# Revit family: IS_iLifeA_T4519_BIM_NL
name_source: partatom
category: Plumbing Fixtures
units: mm (PartAtom-declared; Revit-internal decimal feet)

## family parameters
Always vertical = No
Cut with Voids When Loaded = No
OmniClass Number = 23.45.05.14.14
OmniClass Title = Sinks/Lavatories
Part Type = Normal
Room Calculation Point = No
Round Connector Dimension = Use Diameter
Shared = No
Work Plane-Based = No

## types (2) — shared parameters
Accessories = https://www.idealstandard.nl
Afmetingen = 288 x 360 x 195mm
AfstandsEenheid = Millimeter
Afwerking = Weiß
AreaMeasurement = internal
AreaUnits = Millimeter
Artikelnummer = T451901
Artikelomschrijving = I.life A semi-voetstuk wit - Wit
Artikelreferentie = I.life A semipedestal white
Auteur = Ideal Standard
BIMObjectName = IS_IdealStandard_Pedestalwashbasins_I.life_T4519
BarCode = 8014140485872
Beschrijvinggarantie = Herstellergarantie
Bestanddelen = Halbpodest weiß
BimObjectNaam = IS_IdealStandard_Pedestalwashbasins_I.life_T4519
Brand url = https://www.idealstandard.nl
Color = Weiß
ConnectionType = Plumbing
CurrencyUnit = €
CurrentRevision = 1
Date of publishing = 28/06/2021
Description = I.life A semi-voetstuk wit - Wit
DurationUnit = Years
DuurEenheid = Jaar
Edition number = 1
Eigenschappen = Halbpodest weiß
Features = Halbpodest weiß
Finish = Weiß
GTIN code = https://8014140485872
Garantieonderdelen = 5
Garantieunits = Jaar
Help = https://www.idealstandard.nl
Hoogte = 360.000022888184
Hulp = https://www.idealstandard.nl
IFC Classification = Sanitary Terminal
IfcExportAs = IfcSanitaryTerminalType
IfcExportType = PEDESTAL
Installatieinstructies = https://www.idealstandard.nl
Installation instructions = https://www.idealstandard.nl
InstallationInstructions = https://www.idealstandard.nl
Kleur = Weiß
Lengte = 288 mm
LinearUnits = millimeter
MainColor = Weiß
MaintenanceInformation = https://www.idealstandard.nl
Manufacturer = Ideal Standard
Manufacturer name = Ideal Standard
ManufacturerURL = https://www.idealstandard.nl
Material = Vitrous China
Material main = Vitrous China
Merk = Ideal Standard
Model = T451901
ModelNumber = T451901
ModelReference = I.life A semipedestal white
Montageinstuctie = Wandhangende wastafels
Name = Pedestalwashbasins_I.life_T4519_IdealStandard
NettWeight = 8.3
NominalDepth = 288 mm
NominalHeight = 360 mm
NominalWidth = 195 mm
Normen = Pedestalwashbasins_I.life_T4519_IdealStandard
Ophangingwastafel = Wandhangende wastafels
OppervlakteEenheid = millimeter
Product Guid = c94a09f7-ba16-44c3-a6d5-00d3fe5bc0c7
Product SKU = T4519
Product certification = https://www.idealstandard.nl
Product data url = https://bimobject.com
Product family = I.life
Product group = Semi Pedestal
Product name = I.life A semipedestal white
Product url = https://www.idealstandard.nl
ProductInformation = https://www.idealstandard.nl
ProductSoort = Wastafel
Productinformatie = https://www.idealstandard.nl
QR code = http://bimobject.com
Referentie = I.life A semipedestal white
Revisie = 1
Shape = sculpture
Size = 288 x 360 x 195mm
Space = Internal
SpareParts = https://www.idealstandard.nl
Technical description = https://www.idealstandard.nl
Telefoonnummer = 077 355 08 08
Typeconnectie = loodgieter
Typewastafel = wandhangende wastafel
URL = https://https:
Uniclass2015Beschrijving = Pedestal washbasins
Uniclass2015Code = Pr_40_20_96_63
Uniclass2015Referentie = Pr_40_20_96_63
Uniclass2015Title = Pedestal washbasins
Uniclass2015Version = v1.20
Urlproducent = https://https:
ValutaEenheid = €
Versie = 1
Version = 1
VolumeUnits = liters
Volumeunits = liters
Vorm = beeldhouwwerk
WRASURL = https://www.wrasapprovals.co.uk
WaarborgGarantieInstallatie = https://www.idealstandard.nl
WarrantyDescription = manufacturer warranty
WarrantyDurationParts = 99
WarrantyDurationUnit = years
Wisselstukken = https://www.idealstandard.nl
Youtube clip = https://www.youtube.com
zero-valued in all types: Breedte, BrutoGewicht, Cost, Diepte, DrainSize, GrootteAfvoergat, Nettogewicht, Overloop, Vervangingskosten

## type names (no varying parameters)
- T451901 - I.life A semipedestal white - White 1
- T451901 - I.life A semipedestal white - White

## geometry (parser evidence)
native form markers: Sweep x2
no freeform markers — native parametric forms only
